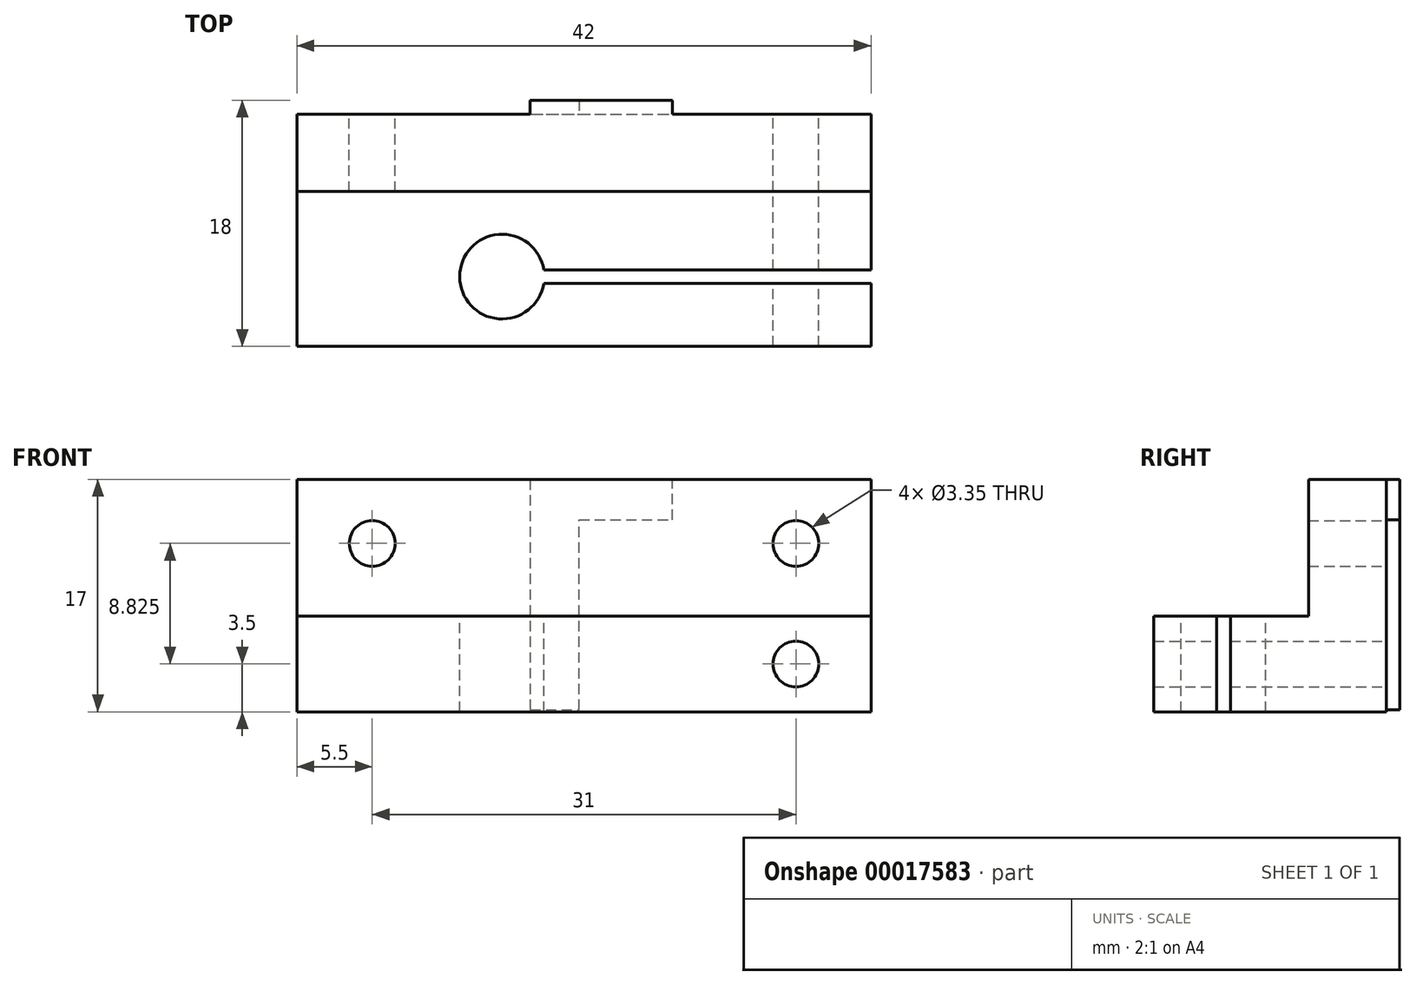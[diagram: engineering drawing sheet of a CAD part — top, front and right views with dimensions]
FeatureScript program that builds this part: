
annotation { "Feature Type Name" : "Feature", "Feature Type Description" : "" }
export const myFeature = defineFeature(function(context is Context, id is Id, definition is map)
    precondition{}
    {
        {
            var Q0;
            Q0=qCreatedBy(makeId("Top.planeOp"),FACE);
            var sketch = newSketch(context, id + "F0", { "sketchPlane" : qUnion([Q0])});
            skLineSegment(sketch, "E0.bottom", {"start": v(0, 0) * mm, "end": v(42, 0) * mm});
            skLineSegment(sketch, "E0.top", {"start": v(0, 17) * mm, "end": v(42, 17) * mm});
            skLineSegment(sketch, "E0.left", {"start": v(0, 0) * mm, "end": v(0, 17) * mm});
            skLineSegment(sketch, "E0.right", {"start": v(42, 0) * mm, "end": v(42, 17) * mm});
            skSolve(sketch);
        }
        {
            var Q0;
            Q0=qSketchRegion(id+"F0",true);
            extrude(context, id + "F1", {"entities" : qUnion([Q0]), "depth" : 7 * mm});
        }
        {
            var Q0;
            Q0=makeQuery(id+"F1.opExtrude","CAP_FACE",FACE,{"disambiguationData":[OSD([sQuery(id+"F0.wireOp",EDGE,"E0.bottom"),sQuery(id+"F0.wireOp",EDGE,"E0.top"),sQuery(id+"F0.wireOp",EDGE,"E0.left"),sQuery(id+"F0.wireOp",EDGE,"E0.right")])],"isStart":false});
            var sketch = newSketch(context, id + "F2", { "sketchPlane" : qUnion([Q0])});
            skCircle(sketch, "E1", {"center": v(15, 5.1) * mm, "radius": 3.1 * mm});
            skLineSegment(sketch, "E2", {"start": v(15, 5.1) * mm, "end": v(42, 5.1) * mm});
            skLineSegment(sketch, "E3", {"start": v(42, 5.1) * mm, "end": v(42, 4.6) * mm});
            skLineSegment(sketch, "E4", {"start": v(42, 4.6) * mm, "end": v(18.06, 4.6) * mm});
            skLineSegment(sketch, "E5", {"start": v(42, 5.1) * mm, "end": v(42, 5.6) * mm});
            skLineSegment(sketch, "E6", {"start": v(42, 5.6) * mm, "end": v(18.06, 5.6) * mm});
            skSolve(sketch);
        }
        {
            var Q0;
            Q0=makeQuery(id+"F1.opExtrude","SWEPT_FACE",FACE,{"disambiguationData":[OSD([sQuery(id+"F0.wireOp",EDGE,"E0.top")])]});
            var sketch = newSketch(context, id + "F3", { "sketchPlane" : qUnion([Q0])});
            skCircle(sketch, "E7", {"center": v(-36.5, 3.5) * mm, "radius": 1.68 * mm});
            skLineSegment(sketch, "E8", {"start": v(-36.5, 3.5) * mm, "end": v(-42, 3.5) * mm});
            skSolve(sketch);
        }
        {
            var Q0;
            Q0=qSketchRegion(id+"F3",true);
            extrude(context, id + "F4", {"entities" : qUnion([Q0]), "operationType" : NewBodyOperationType.REMOVE, "oppositeDirection" : true, "depth" : 25 * mm});
        }
        {
            var Q0;
            Q0=makeQuery(id+"F1.opExtrude","CAP_FACE",FACE,{"disambiguationData":[OSD([sQuery(id+"F0.wireOp",EDGE,"E0.bottom"),sQuery(id+"F0.wireOp",EDGE,"E0.top"),sQuery(id+"F0.wireOp",EDGE,"E0.left"),sQuery(id+"F0.wireOp",EDGE,"E0.right")])],"isStart":false});
            var sketch = newSketch(context, id + "F5", { "sketchPlane" : qUnion([Q0])});
            skLineSegment(sketch, "E9.bottom", {"start": v(0, 17) * mm, "end": v(42, 17) * mm});
            skLineSegment(sketch, "E9.top", {"start": v(0, 11.33) * mm, "end": v(42, 11.33) * mm});
            skLineSegment(sketch, "E9.left", {"start": v(0, 17) * mm, "end": v(0, 11.33) * mm});
            skLineSegment(sketch, "E9.right", {"start": v(42, 17) * mm, "end": v(42, 11.33) * mm});
            skSolve(sketch);
        }
        {
            var Q0;
            Q0=makeQuery(id+"F5.imprint","IMPRINT",FACE,{"disambiguationData":[TD([[makeQuery(id+"F5.imprint","IMPRINT",EDGE,{"derivedFrom":sQuery(id+"F5.wireOp",EDGE,"E9.bottom")}),-1.0]])]});
            extrude(context, id + "F6", {"entities" : qUnion([Q0]), "operationType" : NewBodyOperationType.ADD, "depth" : 10 * mm});
        }
        {
            var Q0;
            Q0=makeQuery(id+"F6.boolean.opBoolean","MERGE",FACE,{"derivedFrom":[makeQuery(id+"F1.opExtrude","SWEPT_FACE",FACE,{"disambiguationData":[OSD([sQuery(id+"F0.wireOp",EDGE,"E0.top")])]}),makeQuery(id+"F6.opExtrude","SWEPT_FACE",FACE,{"disambiguationData":[OSD([sQuery(id+"FFFDCbTcivKPk1C_1.wireOp",EDGE,"d29ae964-e38a-46b3-8ff4-cadffaec6662.bottom")])]})]});
            var sketch = newSketch(context, id + "F7", { "sketchPlane" : qUnion([Q0])});
            skPoint(sketch, "E10", {"position": v(-36.5, 3.5) * mm});
            skCircle(sketch, "E11", {"center": v(-36.5, 12.33) * mm, "radius": 1.68 * mm});
            skCircle(sketch, "E12", {"center": v(-5.5, 12.33) * mm, "radius": 1.68 * mm});
            skSolve(sketch);
        }
        {
            var Q0;
            Q0=qSketchRegion(id+"F7",true);
            extrude(context, id + "F8", {"entities" : qUnion([Q0]), "operationType" : NewBodyOperationType.REMOVE, "oppositeDirection" : true, "depth" : 25 * mm});
        }
        {
            var Q0;
            Q0=qSketchRegion(id+"F2",true);
            extrude(context, id + "F9", {"entities" : qUnion([Q0]), "operationType" : NewBodyOperationType.REMOVE, "oppositeDirection" : true, "depth" : 25 * mm});
        }
        {
            var Q0;
            Q0=makeQuery(id+"F6.boolean.opBoolean","MERGE",FACE,{"derivedFrom":[makeQuery(id+"F1.opExtrude","SWEPT_FACE",FACE,{"disambiguationData":[OSD([sQuery(id+"F0.wireOp",EDGE,"E0.top")])]}),makeQuery(id+"F6.opExtrude","SWEPT_FACE",FACE,{"disambiguationData":[OSD([sQuery(id+"F5.wireOp",EDGE,"E9.bottom")])]})]});
            var sketch = newSketch(context, id + "F10", { "sketchPlane" : qUnion([Q0])});
            skText(sketch, "E13", { "text": "L", "fontName": "OpenSans-Bold.ttf"});
            const initialGuessF10  = {"E13": [-0.01494, 0.017, -1, 0, 0.017]};
            skSetInitialGuess(sketch, initialGuessF10);
            skSolve(sketch);
        }
        {
            var Q0;
            Q0=qSketchRegion(id+"F10",true);
            extrude(context, id + "F11", {"entities" : qUnion([Q0]), "operationType" : NewBodyOperationType.ADD, "depth" : 1 * mm});
        }
    });
